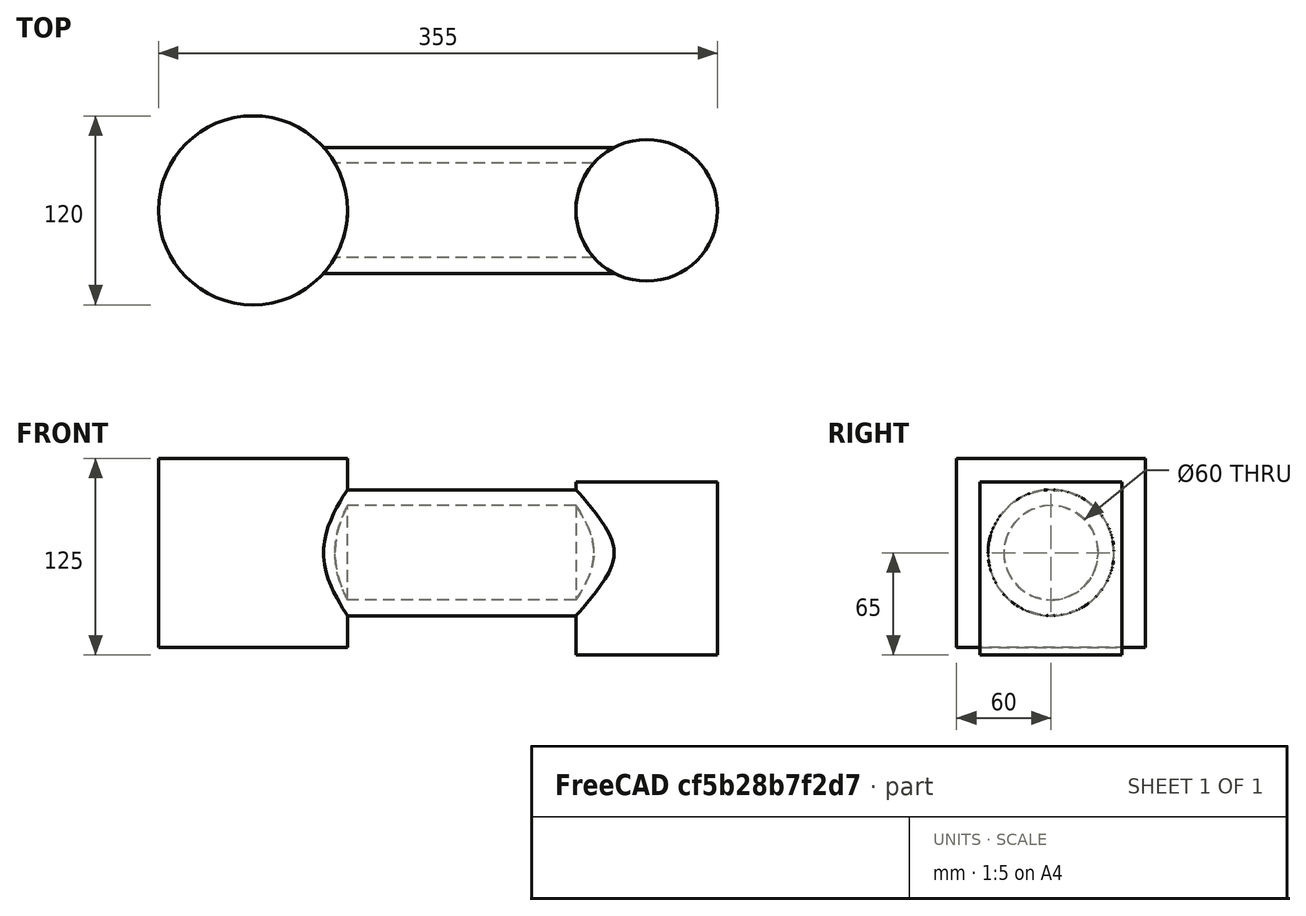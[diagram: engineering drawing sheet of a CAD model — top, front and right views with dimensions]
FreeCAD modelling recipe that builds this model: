
FCSTD DOCUMENT  (FreeCAD 0.19R24366 (Git))
Label: link_2
License: All rights reserved
LicenseURL: http://en.wikipedia.org/wiki/All_rights_reserved
objects: Sketcher::SketchObject×4, PartDesign::Pad×3, PartDesign::Point×2, PartDesign::Revolution×1, PartDesign::Body×1, Mesh::Feature×1
note: 15 computed .brp shape members not serialized (recipe doc carries the construction recipe); baked Part::Feature solids carry a one-line shape summary decoded from their .brp

FEATURE [Sketcher::SketchObject] Sketch
  FullyConstrained = true
  MapMode = 5
  Support = -> [XY_Plane]
  sketch-geometry (4):
    g0: LineSegment StartX=0 StartY=40 StartZ=0 EndX=250 EndY=40 EndZ=0
    g1: LineSegment StartX=250 StartY=40 StartZ=0 EndX=250 EndY=30 EndZ=0
    g2: LineSegment StartX=250 StartY=30 StartZ=0 EndX=0 EndY=30 EndZ=0
    g3: LineSegment StartX=0 StartY=30 StartZ=0 EndX=0 EndY=40 EndZ=0
  constraints (12):
    c: Coincident(g0,g1)
    c: Coincident(g1,g2)
    c: Coincident(g2,g3)
    c: Coincident(g3,g0)
    c: Horizontal(g0)
    c: Horizontal(g2)
    c: Vertical(g1)
    c: Vertical(g3)
    c: PointOnObject(g0,g-2)
    c: DistanceX(g0,g0) = 250
    c: DistanceY(g1,g1) = 10
    c: DistanceY(g-1,g0) = 40
FEATURE [PartDesign::Revolution] Revolution
  Angle = 360
  Axis = (1,0,0)
  Base = (0,0,0)
  Profile = -> Sketch
  ReferenceAxis = -> X_Axis
FEATURE [Sketcher::SketchObject] Sketch001
  FullyConstrained = true
  MapMode = 5
  Support = -> [XY_Plane]
  sketch-geometry (1):
    g0: Circle CenterX=0 CenterY=0 CenterZ=0 NormalX=0 NormalY=0 NormalZ=1 AngleXU=0 Radius=60
  constraints (2):
    c: Coincident(g0,g-1)
    c: Diameter(g0) = 120
FEATURE [PartDesign::Pad] Pad
  BaseFeature = -> Revolution
  Direction = (1,1,1)
  Length = 120
  Length2 = 100
  Midplane = true
  Profile = -> Sketch001
  Type = 0
FEATURE [Sketcher::SketchObject] Sketch002
  ExternalGeometry = -> [Pad]
  FullyConstrained = true
  MapMode = 5
  Support = -> [XY_Plane]
  sketch-geometry (1):
    g0: Circle CenterX=250 CenterY=0 CenterZ=0 NormalX=0 NormalY=0 NormalZ=1 AngleXU=0 Radius=45
  constraints (3):
    c: PointOnObject(g0,g-1)
    c: PointOnObject(g0,g-3)
    c: Diameter(g0) = 90
FEATURE [PartDesign::Pad] Pad001
  BaseFeature = -> Pad
  Direction = (1,1,1)
  Length = 90
  Length2 = 100
  Midplane = true
  Profile = -> Sketch002
  Type = 0
FEATURE [Sketcher::SketchObject] Sketch003
  ExternalGeometry = -> [Pad001]
  FullyConstrained = true
  MapMode = 5
  Placement = pos=(0,0,-45) rot=(1,0,0;3.14159rad)
  Support = -> [Pad001]
  sketch-geometry (1):
    g0: Circle CenterX=250 CenterY=0 CenterZ=0 NormalX=0 NormalY=0 NormalZ=1 AngleXU=0 Radius=45
  constraints (2):
    c: Coincident(g0,g-3)
    c: Equal(g0,g-3)
FEATURE [PartDesign::Pad] Pad002
  BaseFeature = -> Pad001
  Direction = (1,1,1)
  Length = 20
  Length2 = 100
  Profile = -> Sketch003
  Type = 0
FEATURE [PartDesign::Point] DatumPoint
  AttacherType = Attacher::AttachEnginePoint
  MapMode = 36
  Placement = pos=(0,0,-60) rot=(1,0,0;1.5708rad)
  Support = -> [Pad002]
FEATURE [PartDesign::Point] DatumPoint001
  AttacherType = Attacher::AttachEnginePoint
  MapMode = 36
  Placement = pos=(250,0,-65) rot=(-1,0,0;1.5708rad)
  Support = -> [Pad002]
FEATURE [PartDesign::Body] Body
  Group = -> [Sketch,Revolution,Sketch001,Pad,Sketch002,Pad001,Sketch003,Pad002,DatumPoint,DatumPoint001]
  Origin = -> Origin
  Placement = pos=(0,0,60) rot=(0,0,1;0rad)
  Tip = -> Pad002
FEATURE [Mesh::Feature] Mesh  label="Body (Meshed)"
